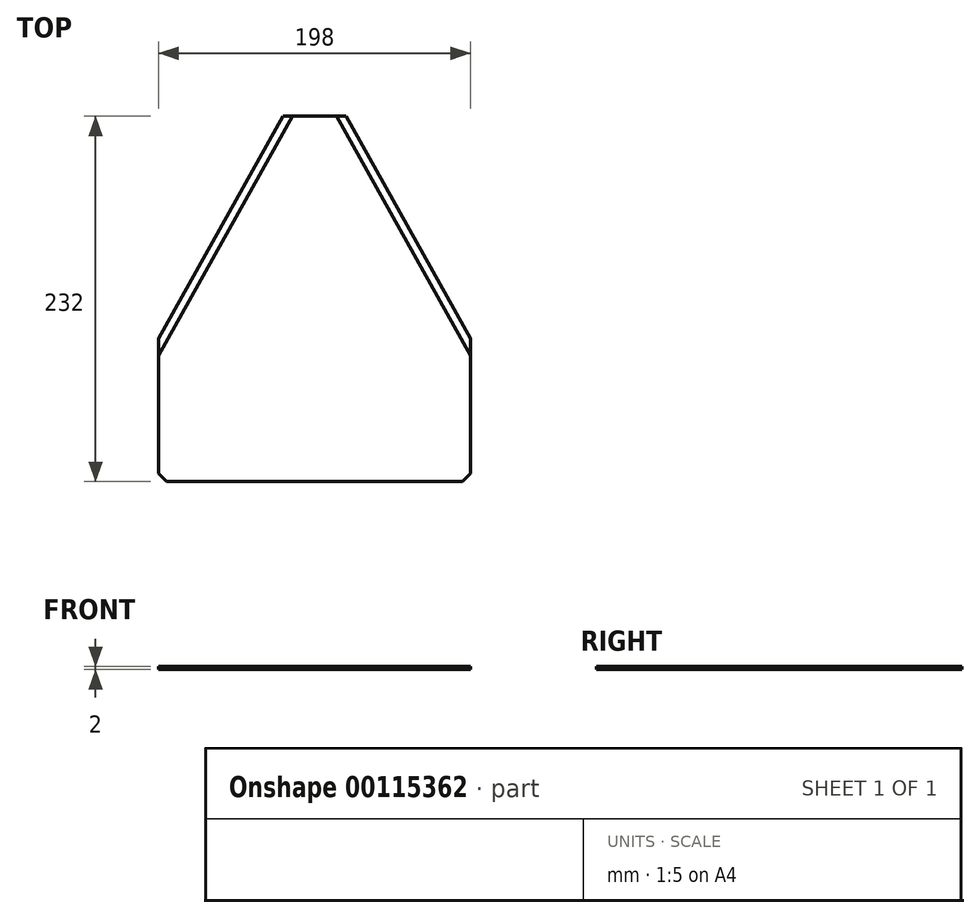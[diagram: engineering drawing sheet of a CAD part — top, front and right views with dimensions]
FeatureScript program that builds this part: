
annotation { "Feature Type Name" : "Feature", "Feature Type Description" : "" }
export const myFeature = defineFeature(function(context is Context, id is Id, definition is map)
    precondition{}
    {
        {
            var Q0;
            Q0=qCreatedBy(makeId("Top.planeOp"),FACE);
            var sketch = newSketch(context, id + "F0", { "sketchPlane" : qUnion([Q0])});
            skLineSegment(sketch, "E0.bottom", {"start": v(-20, 92.92) * mm, "end": v(20, 92.92) * mm});
            skLineSegment(sketch, "E0.top", {"start": v(-94, -139.08) * mm, "end": v(94, -139.08) * mm});
            skLineSegment(sketch, "E1", {"start": v(0, 92.92) * mm, "end": v(0, -139.08) * mm});
            skPoint(sketch, "E1.startSnap0", {"position": v(0, 92.92) * mm});
            skPoint(sketch, "E1.endSnap0", {"position": v(0, -139.08) * mm});
            skLineSegment(sketch, "E2", {"start": v(-99, -59.08) * mm, "end": v(99, -59.08) * mm});
            skLineSegment(sketch, "E3", {"start": v(-20, 92.92) * mm, "end": v(-99, -48.35) * mm});
            skLineSegment(sketch, "E4", {"start": v(20, 92.92) * mm, "end": v(99, -48.35) * mm});
            skLineSegment(sketch, "E5", {"start": v(-14, 92.92) * mm, "end": v(-99, -59.08) * mm});
            skLineSegment(sketch, "E6", {"start": v(14, 92.92) * mm, "end": v(99, -59.08) * mm});
            skLineSegment(sketch, "E7", {"start": v(-99, -59.08) * mm, "end": v(-99, -134.08) * mm});
            skLineSegment(sketch, "E8", {"start": v(99, -59.08) * mm, "end": v(99, -134.08) * mm});
            skPoint(sketch, "E9.orphan", {"position": v(-105, -139.08) * mm});
            skPoint(sketch, "E10.orphan", {"position": v(105, -139.08) * mm});
            skPoint(sketch, "E0.right.start.orphan", {"position": v(105, 92.92) * mm});
            skPoint(sketch, "E0.left.start.orphan", {"position": v(-105, 92.92) * mm});
            skLineSegment(sketch, "E11", {"start": v(-99, -59.08) * mm, "end": v(-99, -48.35) * mm});
            skPoint(sketch, "E12.orphan", {"position": v(-105, -59.08) * mm});
            skLineSegment(sketch, "E13", {"start": v(99, -59.08) * mm, "end": v(99, -48.35) * mm});
            skPoint(sketch, "E14.orphan", {"position": v(105, -59.08) * mm});
            skLineSegment(sketch, "E15", {"start": v(99, -134.08) * mm, "end": v(94, -139.08) * mm});
            skLineSegment(sketch, "E16", {"start": v(-99, -134.08) * mm, "end": v(-94, -139.08) * mm});
            skPoint(sketch, "E17.orphan", {"position": v(99, -139.08) * mm});
            skPoint(sketch, "E18.orphan", {"position": v(-99, -139.08) * mm});
            skSolve(sketch);
        }
        {
            var Q0;
            {var subQ0=sQuery(id+"F0.wireOp",EDGE,"E3");Q0=makeQuery(id+"F0.imprint","IMPRINT",FACE,{"disambiguationData":[TD([[makeQuery(id+"F0.imprint","IMPRINT",EDGE,{"derivedFrom":subQ0}),1.0]])]});}
            var Q1;
            {var subQ3=sQuery(id+"F0.wireOp",EDGE,"E5");Q1=makeQuery(id+"F0.imprint","IMPRINT",FACE,{"disambiguationData":[TD([[makeQuery(id+"F0.imprint","IMPRINT",EDGE,{"derivedFrom":subQ3}),1.0]])]});}
            var Q2;
            {var subQ3=sQuery(id+"F0.wireOp",EDGE,"E6");Q2=makeQuery(id+"F0.imprint","IMPRINT",FACE,{"disambiguationData":[TD([[makeQuery(id+"F0.imprint","IMPRINT",EDGE,{"derivedFrom":subQ3}),-1.0]])]});}
            var Q3;
            {var subQ0=sQuery(id+"F0.wireOp",EDGE,"E4");Q3=makeQuery(id+"F0.imprint","IMPRINT",FACE,{"disambiguationData":[TD([[makeQuery(id+"F0.imprint","IMPRINT",EDGE,{"derivedFrom":subQ0}),-1.0]])]});}
            var Q4;
            {var subQ0=sQuery(id+"F0.wireOp",EDGE,"E8");Q4=makeQuery(id+"F0.imprint","IMPRINT",FACE,{"disambiguationData":[TD([[makeQuery(id+"F0.imprint","IMPRINT",EDGE,{"derivedFrom":subQ0}),-1.0]])]});}
            var Q5;
            {var subQ0=sQuery(id+"F0.wireOp",EDGE,"E7");Q5=makeQuery(id+"F0.imprint","IMPRINT",FACE,{"disambiguationData":[TD([[makeQuery(id+"F0.imprint","IMPRINT",EDGE,{"derivedFrom":subQ0}),1.0]])]});}
            extrude(context, id + "F1", {"entities" : qUnion([Q0, Q1, Q2, Q3, Q4, Q5]), "depth" : 1 * mm});
        }
        {
            var Q0;
            Q0=makeQuery(id+"F1.opExtrude","CAP_FACE",FACE,{"disambiguationData":[OSD([sQuery(id+"F0.wireOp",EDGE,"E0.bottom"),sQuery(id+"F0.wireOp",EDGE,"E0.top"),sQuery(id+"F0.wireOp",EDGE,"E3"),sQuery(id+"F0.wireOp",EDGE,"E4"),sQuery(id+"F0.wireOp",EDGE,"E7"),sQuery(id+"F0.wireOp",EDGE,"E8"),sQuery(id+"F0.wireOp",EDGE,"E11"),sQuery(id+"F0.wireOp",EDGE,"E13"),sQuery(id+"F0.wireOp",EDGE,"E15"),sQuery(id+"F0.wireOp",EDGE,"E16")])],"isStart":false});
            var sketch = newSketch(context, id + "F2", { "sketchPlane" : qUnion([Q0])});
            skLineSegment(sketch, "E19", {"start": v(-14, 92.92) * mm, "end": v(-99, -59.08) * mm});
            skLineSegment(sketch, "E20", {"start": v(14, 92.92) * mm, "end": v(99, -59.08) * mm});
            skSolve(sketch);
        }
        {
            var Q0;
            {var subQ3=sQuery(id+"F2.wireOp",EDGE,"E19");Q0=makeQuery(id+"F2.imprint","IMPRINT",FACE,{"disambiguationData":[TD([[makeQuery(id+"F2.imprint","IMPRINT",EDGE,{"derivedFrom":subQ3}),1.0]])]});}
            extrude(context, id + "F3", {"entities" : qUnion([Q0]), "operationType" : NewBodyOperationType.ADD, "depth" : 1 * mm});
        }
    });
